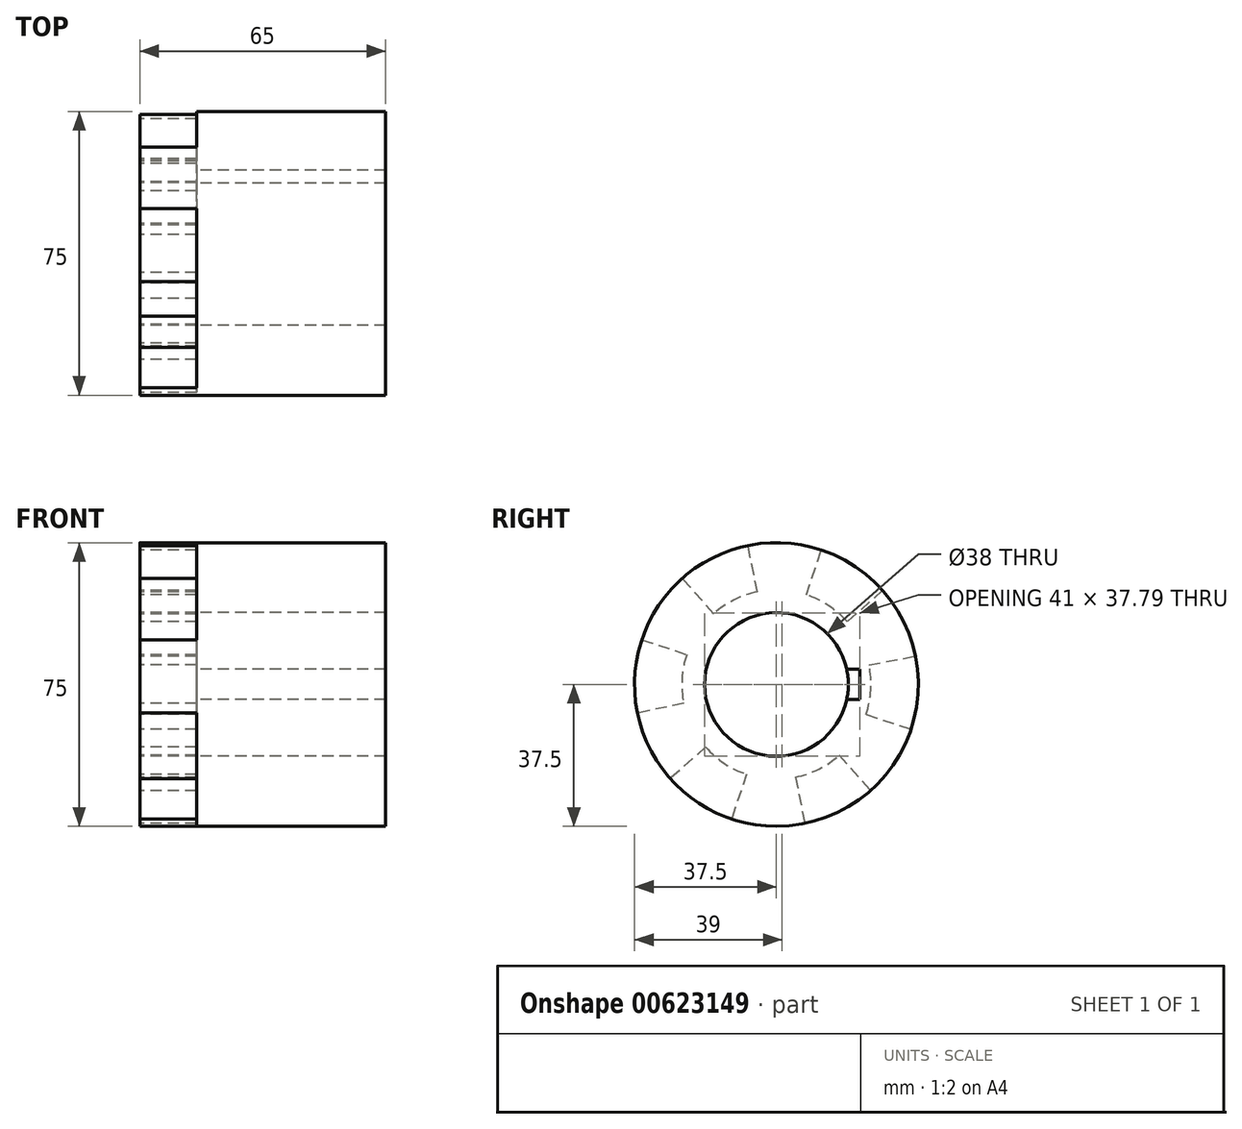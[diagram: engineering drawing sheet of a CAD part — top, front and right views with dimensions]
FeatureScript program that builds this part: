
annotation { "Feature Type Name" : "Feature", "Feature Type Description" : "" }
export const myFeature = defineFeature(function(context is Context, id is Id, definition is map)
    precondition{}
    {
        {
            var Q0;
            Q0=qCreatedBy(makeId("Right.planeOp"),FACE);
            cPlane(context, id + "F0", {"entities" : qUnion([Q0]), "cplaneType" : CPlaneType.OFFSET, "offset" : 15 * mm, "width" : 150 * mm, "height" : 150 * mm});
        }
        {
            var Q0;
            Q0=qCreatedBy(id+"F0.planeOp",FACE);
            var sketch = newSketch(context, id + "F1", { "sketchPlane" : qUnion([Q0])});
            skArc(sketch, "E0", {"start": v(18.57, 4) * mm, "mid": v(-19, 0) * mm, "end": v(18.57, -4) * mm});
            skCircle(sketch, "E1", {"center": v(0, 0) * mm, "radius": 37.5 * mm});
            skPoint(sketch, "E2", {"position": v(22, 0) * mm});
            skLineSegment(sketch, "E3", {"start": v(22, 4) * mm, "end": v(22, -4) * mm});
            skLineSegment(sketch, "E4", {"start": v(22, 4) * mm, "end": v(18.57, 4) * mm});
            skLineSegment(sketch, "E5", {"start": v(22, -4) * mm, "end": v(18.57, -4) * mm});
            skSolve(sketch);
        }
        {
            var Q0;
            Q0=makeQuery(id+"F1.imprint","IMPRINT",FACE,{"disambiguationData":[TD([[makeQuery(id+"F1.imprint","IMPRINT",EDGE,{"derivedFrom":sQuery(id+"F1.wireOp",EDGE,"E0")}),-1.0]])]});
            extrude(context, id + "F2", {"entities" : qUnion([Q0]), "depth" : 50 * mm, "offsetDistance" : 25 * mm});
        }
        {
            var Q0;
            Q0=qCreatedBy(makeId("Right.planeOp"),FACE);
            var sketch = newSketch(context, id + "F3", { "sketchPlane" : qUnion([Q0])});
            skCircle(sketch, "E6.0", {"center": v(0, 0) * mm, "radius": 37.5 * mm});
            skLineSegment(sketch, "E7", {"start": v(0, 0) * mm, "end": v(-11.85, -35.58) * mm, "construction": true});
            skLineSegment(sketch, "E8", {"start": v(0, 0) * mm, "end": v(7.52, -36.74) * mm, "construction": true});
            skLineSegment(sketch, "E9", {"start": v(0, 0) * mm, "end": v(24.88, -28.05) * mm, "construction": true});
            skLineSegment(sketch, "E10", {"start": v(0, 0) * mm, "end": v(35.58, -11.85) * mm, "construction": true});
            skLineSegment(sketch, "E11", {"start": v(0, 0) * mm, "end": v(36.74, 7.52) * mm, "construction": true});
            skLineSegment(sketch, "E12", {"start": v(0, 0) * mm, "end": v(28.05, 24.88) * mm, "construction": true});
            skLineSegment(sketch, "E13", {"start": v(0, 0) * mm, "end": v(11.85, 35.58) * mm, "construction": true});
            skLineSegment(sketch, "E14", {"start": v(0, 0) * mm, "end": v(-7.52, 36.74) * mm, "construction": true});
            skLineSegment(sketch, "E15", {"start": v(0, 0) * mm, "end": v(-35.58, 11.85) * mm, "construction": true});
            skLineSegment(sketch, "E16", {"start": v(0, 0) * mm, "end": v(-28.05, -24.88) * mm, "construction": true});
            skLineSegment(sketch, "E17", {"start": v(0, 0) * mm, "end": v(-36.74, -7.52) * mm, "construction": true});
            skLineSegment(sketch, "E18", {"start": v(0, 0) * mm, "end": v(-24.88, 28.05) * mm, "construction": true});
            skLineSegment(sketch, "E19", {"start": v(3.76, -18.37) * mm, "end": v(7.52, -36.74) * mm});
            skLineSegment(sketch, "E20", {"start": v(12.44, -14.03) * mm, "end": v(24.88, -28.05) * mm});
            skLineSegment(sketch, "E21", {"start": v(-18.37, -3.76) * mm, "end": v(-36.74, -7.52) * mm});
            skLineSegment(sketch, "E22", {"start": v(-35.58, 11.85) * mm, "end": v(-17.79, 5.93) * mm});
            skLineSegment(sketch, "E23", {"start": v(5.93, 17.79) * mm, "end": v(11.85, 35.58) * mm});
            skLineSegment(sketch, "E24", {"start": v(28.05, 24.88) * mm, "end": v(14.03, 12.44) * mm});
            skPoint(sketch, "E25.orphan", {"position": v(18.57, -4) * mm});
            skArc(sketch, "E26.converted", {"start": v(18.61, 3.81) * mm, "mid": v(18.6, 3.9) * mm, "end": v(18.57, 4) * mm});
            skPoint(sketch, "E27.orphan", {"position": v(18.57, 4) * mm});
            skLineSegment(sketch, "E28", {"start": v(18.03, -6) * mm, "end": v(35.58, -11.85) * mm});
            skLineSegment(sketch, "E29", {"start": v(-6, -18.03) * mm, "end": v(-11.85, -35.58) * mm});
            skLineSegment(sketch, "E30", {"start": v(-13.36, -11.85) * mm, "end": v(-28.05, -24.88) * mm});
            skLineSegment(sketch, "E31", {"start": v(-12.6, 14.21) * mm, "end": v(-24.88, 28.05) * mm});
            skLineSegment(sketch, "E32", {"start": v(-3.76, 18.37) * mm, "end": v(-7.52, 36.74) * mm});
            skLineSegment(sketch, "E33", {"start": v(18.57, 4) * mm, "end": v(36.74, 7.52) * mm});
            skArc(sketch, "E34", {"start": v(5.02, -24.5) * mm, "mid": v(11.18, -22.36) * mm, "end": v(16.59, -18.7) * mm});
            skArc(sketch, "E35", {"start": v(18.7, 16.59) * mm, "mid": v(13.77, 20.86) * mm, "end": v(7.9, 23.72) * mm});
            skArc(sketch, "E36", {"start": v(-23.72, 7.9) * mm, "mid": v(-24.96, 1.5) * mm, "end": v(-24.5, -5.02) * mm});
            skCircle(sketch, "E37", {"center": v(0, 0) * mm, "radius": 19 * mm});
            skCircle(sketch, "E38", {"center": v(0, 0) * mm, "radius": 25 * mm});
            skSolve(sketch);
        }
        {
            var Q0;
            {var subQ0=sQuery(id+"F3.wireOp",EDGE,"E20");var subQ1=sQuery(id+"F3.wireOp",EDGE,"E6.0");var subQ2=makeQuery(id+"F3.imprint","INTERSECT",VERTEX,{"derivedFrom":[subQ1,subQ0]});Q0=makeQuery(id+"F3.imprint","IMPRINT",FACE,{"disambiguationData":[TD([[makeQuery(id+"F3.imprint","IMPRINT",EDGE,{"disambiguationData":[TD([[subQ2,1.0]])],"derivedFrom":subQ1}),1.0]])]});}
            var Q1;
            {var subQ0=sQuery(id+"F3.wireOp",EDGE,"E22");var subQ1=sQuery(id+"F3.wireOp",EDGE,"E6.0");var subQ2=makeQuery(id+"F3.imprint","INTERSECT",VERTEX,{"derivedFrom":[subQ1,subQ0]});Q1=makeQuery(id+"F3.imprint","IMPRINT",FACE,{"disambiguationData":[TD([[makeQuery(id+"F3.imprint","IMPRINT",EDGE,{"disambiguationData":[TD([[subQ2,-1.0]])],"derivedFrom":subQ1}),1.0]])]});}
            var Q2;
            {var subQ0=sQuery(id+"F3.wireOp",EDGE,"E24");var subQ1=sQuery(id+"F3.wireOp",EDGE,"E6.0");var subQ2=makeQuery(id+"F3.imprint","INTERSECT",VERTEX,{"derivedFrom":[subQ1,subQ0]});Q2=makeQuery(id+"F3.imprint","IMPRINT",FACE,{"disambiguationData":[TD([[makeQuery(id+"F3.imprint","IMPRINT",EDGE,{"disambiguationData":[TD([[subQ2,-1.0]])],"derivedFrom":subQ1}),1.0]])]});}
            var Q3;
            Q3=makeQuery(id+"F2.opExtrude","CAP_FACE",FACE,{"disambiguationData":[OSD([sQuery(id+"F1.wireOp",EDGE,"E0"),sQuery(id+"F1.wireOp",EDGE,"E1"),sQuery(id+"F1.wireOp",EDGE,"E3"),sQuery(id+"F1.wireOp",EDGE,"E4"),sQuery(id+"F1.wireOp",EDGE,"E5")])],"isStart":true});
            extrude(context, id + "F4", {"entities" : qUnion([Q0, Q1, Q2]), "operationType" : NewBodyOperationType.ADD, "endBound" : BoundingType.UP_TO_NEXT, "depth" : 25 * mm, "endBoundEntityFace" : qUnion([Q3]), "offsetDistance" : 25 * mm});
        }
        {
            var Q0;
            {var subQ0=sQuery(id+"F3.wireOp",EDGE,"E23");var subQ1=sQuery(id+"F3.wireOp",EDGE,"E6.0");var subQ2=makeQuery(id+"F3.imprint","INTERSECT",VERTEX,{"derivedFrom":[subQ1,subQ0]});Q0=makeQuery(id+"F3.imprint","IMPRINT",FACE,{"disambiguationData":[TD([[makeQuery(id+"F3.imprint","IMPRINT",EDGE,{"disambiguationData":[TD([[subQ2,-1.0]])],"derivedFrom":subQ1}),1.0]])]});}
            var Q1;
            {var subQ0=sQuery(id+"F3.wireOp",EDGE,"E22");var subQ1=sQuery(id+"F3.wireOp",EDGE,"E6.0");var subQ2=makeQuery(id+"F3.imprint","INTERSECT",VERTEX,{"derivedFrom":[subQ1,subQ0]});Q1=makeQuery(id+"F3.imprint","IMPRINT",FACE,{"disambiguationData":[TD([[makeQuery(id+"F3.imprint","IMPRINT",EDGE,{"disambiguationData":[TD([[subQ2,1.0]])],"derivedFrom":subQ1}),1.0]])]});}
            var Q2;
            {var subQ0=sQuery(id+"F3.wireOp",EDGE,"E21");var subQ1=sQuery(id+"F3.wireOp",EDGE,"E6.0");var subQ2=makeQuery(id+"F3.imprint","INTERSECT",VERTEX,{"derivedFrom":[subQ1,subQ0]});Q2=makeQuery(id+"F3.imprint","IMPRINT",FACE,{"disambiguationData":[TD([[makeQuery(id+"F3.imprint","IMPRINT",EDGE,{"disambiguationData":[TD([[subQ2,-1.0]])],"derivedFrom":subQ1}),1.0]])]});}
            var Q3;
            {var subQ0=sQuery(id+"F3.wireOp",EDGE,"E19");var subQ1=sQuery(id+"F3.wireOp",EDGE,"E6.0");var subQ2=makeQuery(id+"F3.imprint","INTERSECT",VERTEX,{"derivedFrom":[subQ1,subQ0]});Q3=makeQuery(id+"F3.imprint","IMPRINT",FACE,{"disambiguationData":[TD([[makeQuery(id+"F3.imprint","IMPRINT",EDGE,{"disambiguationData":[TD([[subQ2,1.0]])],"derivedFrom":subQ1}),1.0]])]});}
            var Q4;
            {var subQ0=sQuery(id+"F3.wireOp",EDGE,"E20");var subQ1=sQuery(id+"F3.wireOp",EDGE,"E6.0");var subQ2=makeQuery(id+"F3.imprint","INTERSECT",VERTEX,{"derivedFrom":[subQ1,subQ0]});Q4=makeQuery(id+"F3.imprint","IMPRINT",FACE,{"disambiguationData":[TD([[makeQuery(id+"F3.imprint","IMPRINT",EDGE,{"disambiguationData":[TD([[subQ2,-1.0]])],"derivedFrom":subQ1}),1.0]])]});}
            var Q5;
            {var subQ0=sQuery(id+"F3.wireOp",EDGE,"E24");var subQ1=sQuery(id+"F3.wireOp",EDGE,"E6.0");var subQ2=makeQuery(id+"F3.imprint","INTERSECT",VERTEX,{"derivedFrom":[subQ1,subQ0]});Q5=makeQuery(id+"F3.imprint","IMPRINT",FACE,{"disambiguationData":[TD([[makeQuery(id+"F3.imprint","IMPRINT",EDGE,{"disambiguationData":[TD([[subQ2,1.0]])],"derivedFrom":subQ1}),1.0]])]});}
            var Q6;
            {var subQ1=sQuery(id+"F3.wireOp",EDGE,"E24");var subQ3=sQuery(id+"F3.wireOp",EDGE,"E37");var subQ4=makeQuery(id+"F3.imprint","INTERSECT",VERTEX,{"derivedFrom":[subQ1,subQ3]});Q6=makeQuery(id+"F3.imprint","IMPRINT",FACE,{"disambiguationData":[TD([[makeQuery(id+"F3.imprint","IMPRINT",EDGE,{"disambiguationData":[TD([[subQ4,1.0]])],"derivedFrom":subQ1}),1.0]])]});}
            var Q7;
            {var subQ1=sQuery(id+"F3.wireOp",EDGE,"E35");Q7=makeQuery(id+"F3.imprint","IMPRINT",FACE,{"disambiguationData":[TD([[makeQuery(id+"F3.imprint","IMPRINT",EDGE,{"derivedFrom":subQ1}),1.0]])]});}
            var Q8;
            {var subQ0=sQuery(id+"F3.wireOp",EDGE,"E38");var subQ5=sQuery(id+"F3.wireOp",EDGE,"E32");var subQ7=makeQuery(id+"F3.imprint","INTERSECT",VERTEX,{"derivedFrom":[subQ5,subQ0]});Q8=makeQuery(id+"F3.imprint","IMPRINT",FACE,{"disambiguationData":[TD([[makeQuery(id+"F3.imprint","IMPRINT",EDGE,{"disambiguationData":[TD([[subQ7,1.0]])],"derivedFrom":subQ5}),-1.0]])]});}
            var Q9;
            {var subQ0=sQuery(id+"F3.wireOp",EDGE,"E38");var subQ1=sQuery(id+"F3.wireOp",EDGE,"E31");var subQ2=makeQuery(id+"F3.imprint","INTERSECT",VERTEX,{"derivedFrom":[subQ1,subQ0]});Q9=makeQuery(id+"F3.imprint","IMPRINT",FACE,{"disambiguationData":[TD([[makeQuery(id+"F3.imprint","IMPRINT",EDGE,{"disambiguationData":[TD([[subQ2,1.0]])],"derivedFrom":subQ1}),-1.0]])]});}
            var Q10;
            {var subQ0=sQuery(id+"F3.wireOp",EDGE,"E38");var subQ5=sQuery(id+"F3.wireOp",EDGE,"E31");var subQ6=makeQuery(id+"F3.imprint","INTERSECT",VERTEX,{"derivedFrom":[subQ5,subQ0]});Q10=makeQuery(id+"F3.imprint","IMPRINT",FACE,{"disambiguationData":[TD([[makeQuery(id+"F3.imprint","IMPRINT",EDGE,{"disambiguationData":[TD([[subQ6,1.0]])],"derivedFrom":subQ5}),1.0]])]});}
            var Q11;
            {var subQ1=sQuery(id+"F3.wireOp",EDGE,"E36");Q11=makeQuery(id+"F3.imprint","IMPRINT",FACE,{"disambiguationData":[TD([[makeQuery(id+"F3.imprint","IMPRINT",EDGE,{"derivedFrom":subQ1}),1.0]])]});}
            var Q12;
            {var subQ0=sQuery(id+"F3.wireOp",EDGE,"E38");var subQ5=sQuery(id+"F3.wireOp",EDGE,"E30");var subQ6=makeQuery(id+"F3.imprint","INTERSECT",VERTEX,{"derivedFrom":[subQ5,subQ0]});Q12=makeQuery(id+"F3.imprint","IMPRINT",FACE,{"disambiguationData":[TD([[makeQuery(id+"F3.imprint","IMPRINT",EDGE,{"disambiguationData":[TD([[subQ6,1.0]])],"derivedFrom":subQ5}),-1.0]])]});}
            var Q13;
            {var subQ0=sQuery(id+"F3.wireOp",EDGE,"E38");var subQ1=sQuery(id+"F3.wireOp",EDGE,"E29");var subQ2=makeQuery(id+"F3.imprint","INTERSECT",VERTEX,{"derivedFrom":[subQ1,subQ0]});Q13=makeQuery(id+"F3.imprint","IMPRINT",FACE,{"disambiguationData":[TD([[makeQuery(id+"F3.imprint","IMPRINT",EDGE,{"disambiguationData":[TD([[subQ2,1.0]])],"derivedFrom":subQ1}),-1.0]])]});}
            var Q14;
            {var subQ0=sQuery(id+"F3.wireOp",EDGE,"E38");var subQ5=sQuery(id+"F3.wireOp",EDGE,"E29");var subQ6=makeQuery(id+"F3.imprint","INTERSECT",VERTEX,{"derivedFrom":[subQ5,subQ0]});Q14=makeQuery(id+"F3.imprint","IMPRINT",FACE,{"disambiguationData":[TD([[makeQuery(id+"F3.imprint","IMPRINT",EDGE,{"disambiguationData":[TD([[subQ6,1.0]])],"derivedFrom":subQ5}),1.0]])]});}
            var Q15;
            {var subQ1=sQuery(id+"F3.wireOp",EDGE,"E34");Q15=makeQuery(id+"F3.imprint","IMPRINT",FACE,{"disambiguationData":[TD([[makeQuery(id+"F3.imprint","IMPRINT",EDGE,{"derivedFrom":subQ1}),1.0]])]});}
            var Q16;
            {var subQ0=sQuery(id+"F3.wireOp",EDGE,"E38");var subQ5=sQuery(id+"F3.wireOp",EDGE,"E28");var subQ6=makeQuery(id+"F3.imprint","INTERSECT",VERTEX,{"derivedFrom":[subQ5,subQ0]});Q16=makeQuery(id+"F3.imprint","IMPRINT",FACE,{"disambiguationData":[TD([[makeQuery(id+"F3.imprint","IMPRINT",EDGE,{"disambiguationData":[TD([[subQ6,1.0]])],"derivedFrom":subQ5}),-1.0]])]});}
            var Q17;
            {var subQ5=sQuery(id+"F3.wireOp",EDGE,"E26.converted");Q17=makeQuery(id+"F3.imprint","IMPRINT",FACE,{"disambiguationData":[TD([[makeQuery(id+"F3.imprint","IMPRINT",EDGE,{"derivedFrom":subQ5}),-1.0]])]});}
            var Q18;
            Q18=makeQuery(id+"F2.opExtrude","CAP_FACE",FACE,{"disambiguationData":[OSD([sQuery(id+"F1.wireOp",EDGE,"E0"),sQuery(id+"F1.wireOp",EDGE,"E1"),sQuery(id+"F1.wireOp",EDGE,"E3"),sQuery(id+"F1.wireOp",EDGE,"E4"),sQuery(id+"F1.wireOp",EDGE,"E5")])],"isStart":true});
            extrude(context, id + "F5", {"entities" : qUnion([Q0, Q1, Q2, Q3, Q4, Q5, Q6, Q7, Q8, Q9, Q10, Q11, Q12, Q13, Q14, Q15, Q16, Q17]), "endBound" : BoundingType.UP_TO_SURFACE, "depth" : 25 * mm, "endBoundEntityFace" : qUnion([Q18]), "offsetDistance" : 25 * mm});
        }
    });
